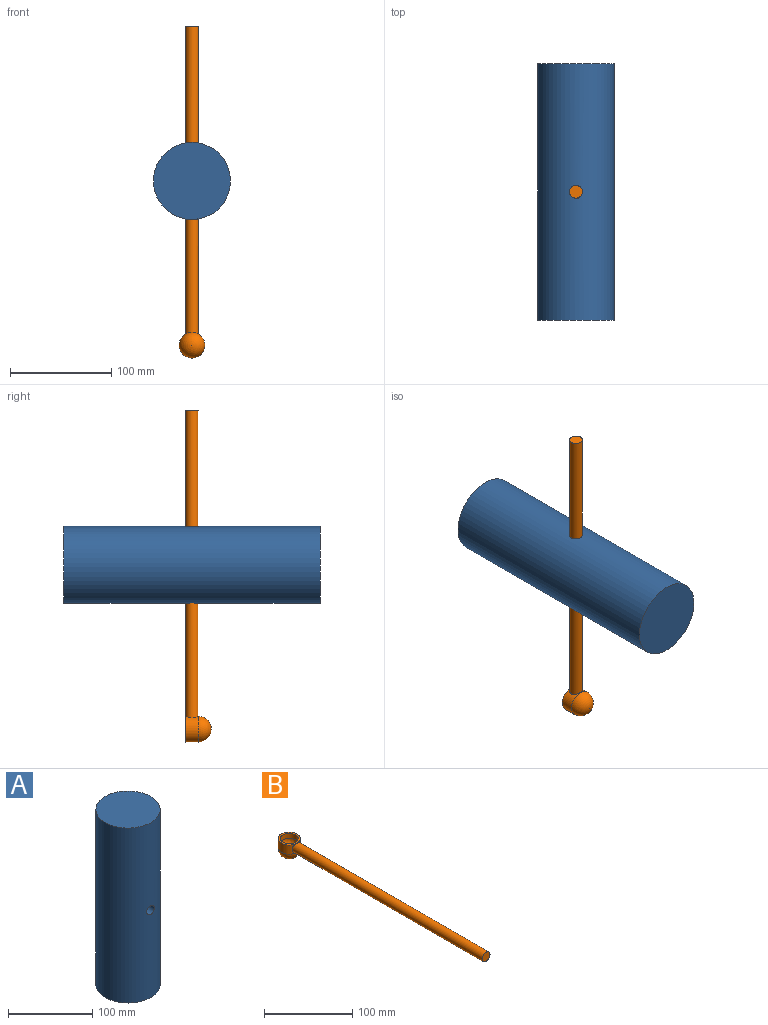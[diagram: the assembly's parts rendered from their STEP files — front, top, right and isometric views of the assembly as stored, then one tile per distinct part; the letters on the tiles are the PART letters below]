
ASSEMBLY  parts=2 mates=1
PART A: 4 faces, bbox 76.2x76.2x254 mm
  f0: cylinder r=38.1mm len=254mm, axis (0,0,-1), area 60549.3mm2, adj f1,f2,f3
  f1: plane 76.2x76.2mm, normal (0,0,1), area 4560.4mm2, adj f0
  f2: plane 76.2x76.2mm, normal (0,0,-1), area 4560.4mm2, adj f0
  f3: cylinder r=6.35mm len=76.2mm, axis (0,-1,0), area 3019mm2, adj f0
PART B: 8 faces, bbox 25.4x328.5x25.4 mm
  f0: plane 12.7x12.7mm, normal (0,-1,0), area 126.7mm2, adj f7
  f1: plane 25.4x25.4mm, normal (0,0,1), area 182.4mm2, adj f2,f3
  f2: cylinder r=12.7mm len=25.4mm, axis (0,0,1), area 882.4mm2, adj f1,f6,f7
  f3: cylinder r=10.16mm len=20.32mm, axis (0,0,1), area 445.9mm2, adj f1,f5
  f4: plane 1.27x1.27mm, normal (0,0,1), area 1.3mm2, adj f5
  f5: torus R=0.64mm, axis (0,0,1), area 629.7mm2, adj f3,f4
  f6: sphere r=12.7mm, area 1013.4mm2, adj f2
  f7: cylinder r=6.35mm len=304.8mm, axis (0,1,0), area 12126.4mm2, adj f0,f2
PLACE A rot(axis=(-1,0,0),90deg) t=(0,-254,0)mm
PLACE B rot(axis=(-1,0,0),90deg) t=(0,-120.65,-119.02)mm
MATE fastened A.f3 <-> B.f7  axis (0,0,1) through (0,-127,0)mm
